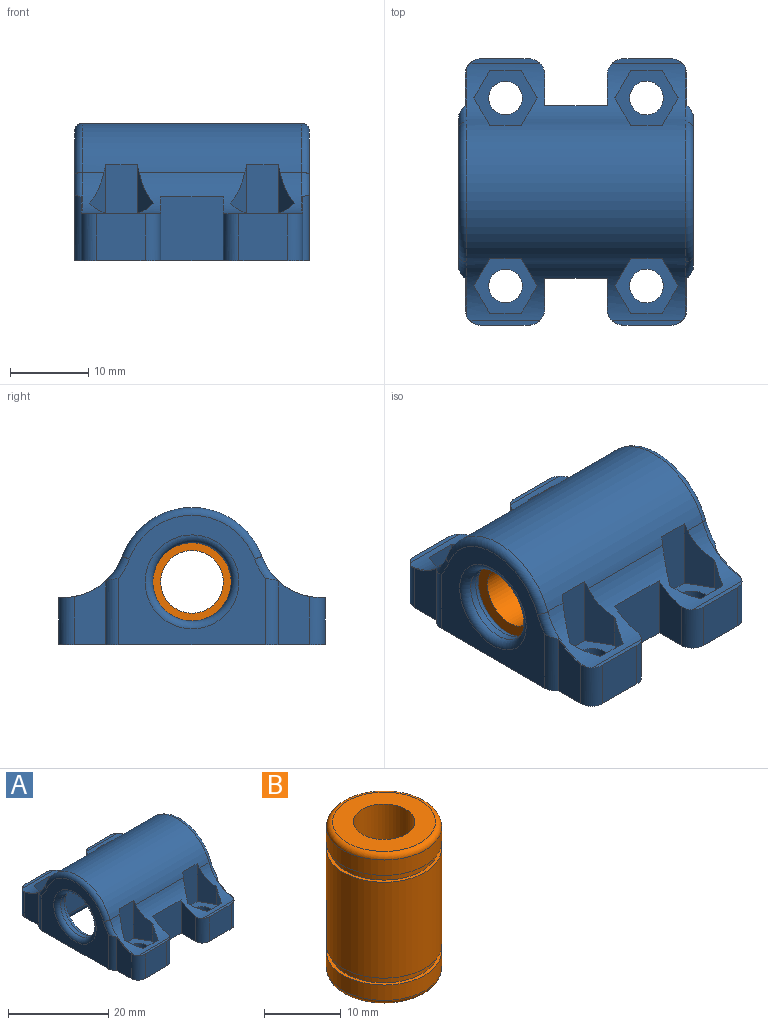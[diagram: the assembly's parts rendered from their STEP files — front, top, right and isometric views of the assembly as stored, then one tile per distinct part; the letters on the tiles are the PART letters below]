
ASSEMBLY  parts=2 mates=1
PART A: 94 faces, bbox 30x34x18.3 mm
  f0: cylinder r=2.15mm len=4.3mm, axis (0,0,-1), area 40.5mm2, adj f14,f88
  f1: cylinder r=2.15mm len=4.3mm, axis (0,0,-1), area 40.5mm2, adj f14,f61
  f2: cylinder r=2.15mm len=4.3mm, axis (0,0,-1), area 40.5mm2, adj f14,f74
  f3: cylinder r=2.15mm len=4.3mm, axis (0,0,-1), area 40.5mm2, adj f14,f75
  f4: plane 8.93x0.56mm, normal (0,0,1), area 4.5mm2, adj f7,f34,f38,f50
  f5: plane 8.93x0.56mm, normal (0,0,1), area 4.5mm2, adj f10,f42,f43,f49
  f6: plane 18.73x16.5mm, normal (-1,0,0), area 152.4mm2, adj f14,f36,f41,f51,f52,f53,f59
  f7: plane 6.15x6mm, normal (0,-1,0), area 36.9mm2, adj f4,f14,f34,f38
  f8: plane 6.15x6mm, normal (0,-1,0), area 36.9mm2, adj f13,f14,f35,f37
  f9: plane 18.73x16.5mm, normal (1,0,0), area 152.4mm2, adj f14,f33,f40,f54,f55,f56,f58
  f10: plane 6.15x6mm, normal (0,1,0), area 36.9mm2, adj f5,f14,f42,f43
  f11: plane 6.15x6mm, normal (0,1,0), area 36.9mm2, adj f12,f14,f39,f44
  f12: plane 8.93x0.56mm, normal (0,0,1), area 4.5mm2, adj f11,f39,f44,f49
  f13: plane 8.93x0.56mm, normal (0,0,1), area 4.5mm2, adj f8,f35,f37,f50
  f14: plane 34x30mm, normal (0,0,-1), area 298.4mm2, adj f0,f1,f2,f3,f6,f7,f8,f9
  f15: plane 24.2x6mm, normal (0,1,0), area 145.2mm2, adj f17,f20,f22,f47
  f16: plane 24.2x6mm, normal (0,-1,0), area 145.2mm2, adj f17,f20,f22,f46
  f17: cylinder r=7.55mm len=24.2mm, axis (-1,0,0), area 446.8mm2, adj f15,f16,f20,f22,f89,f90,f92,f93
  f18: cylinder r=9.5mm len=28mm, axis (-1,0,0), area 631.1mm2, adj f49,f50,f52,f55,f65,f66,f67,f71
  f19: cylinder r=5mm len=10mm, axis (-1,0,0), area 28.3mm2, adj f59,f60
  f20: plane 15.1x13.55mm, normal (1,0,0), area 67mm2, adj f15,f16,f17,f45,f60
  f21: cylinder r=5mm len=10mm, axis (1,0,0), area 28.3mm2, adj f57,f58
  f22: plane 15.1x13.55mm, normal (-1,0,0), area 67mm2, adj f15,f16,f17,f48,f57
  f23: plane 8.13x4mm, normal (1,0,0), area 27.6mm2, adj f14,f24,f43,f49
  f24: plane 8.13x8mm, normal (0,1,0), area 65.1mm2, adj f14,f23,f25,f49
  f25: plane 8.13x4mm, normal (-1,0,0), area 27.6mm2, adj f14,f24,f44,f49
  f26: plane 8.12x4mm, normal (1,0,0), area 27.5mm2, adj f14,f33,f34,f56
  f27: plane 8.12x4mm, normal (-1,0,0), area 27.5mm2, adj f14,f35,f36,f53
  f28: plane 8.13x4mm, normal (-1,0,0), area 27.6mm2, adj f14,f29,f38,f50
  f29: plane 8.13x8mm, normal (0,-1,0), area 65.1mm2, adj f14,f28,f30,f50
  f30: plane 8.13x4mm, normal (1,0,0), area 27.6mm2, adj f14,f29,f37,f50
  f31: plane 8.12x4mm, normal (1,0,0), area 27.5mm2, adj f14,f39,f40,f54
  f32: plane 8.12x4mm, normal (-1,0,0), area 27.5mm2, adj f14,f41,f42,f51
  f33: cylinder r=2mm len=8.44mm, axis (0,0,1), area 15.9mm2, adj f9,f14,f26,f56
  f34: cylinder r=2mm len=6.12mm, axis (0,0,-1), area 18.9mm2, adj f4,f7,f14,f26,f50,f56
  f35: cylinder r=2mm len=6.12mm, axis (0,0,1), area 18.9mm2, adj f8,f13,f14,f27,f50,f53
  f36: cylinder r=2mm len=8.44mm, axis (0,0,-1), area 15.9mm2, adj f6,f14,f27,f53
  f37: cylinder r=2mm len=6.13mm, axis (0,0,-1), area 18.9mm2, adj f8,f13,f14,f30,f50
  f38: cylinder r=2mm len=6.13mm, axis (0,0,1), area 18.9mm2, adj f4,f7,f14,f28,f50
  f39: cylinder r=2mm len=6.12mm, axis (0,0,-1), area 18.9mm2, adj f11,f12,f14,f31,f49,f54
  f40: cylinder r=2mm len=8.44mm, axis (0,0,-1), area 15.9mm2, adj f9,f14,f31,f54
  f41: cylinder r=2mm len=8.44mm, axis (0,0,1), area 15.9mm2, adj f6,f14,f32,f51
  f42: cylinder r=2mm len=6.12mm, axis (0,0,1), area 18.9mm2, adj f5,f10,f14,f32,f49,f51
  f43: cylinder r=2mm len=6.13mm, axis (0,0,-1), area 18.9mm2, adj f5,f10,f14,f23,f49
  f44: cylinder r=2mm len=6.13mm, axis (0,0,1), area 18.9mm2, adj f11,f12,f14,f25,f49
  f45: cylinder r=2mm len=19.1mm, axis (0,-1,0), area 52mm2, adj f14,f20,f46,f47
  f46: cylinder r=2mm len=28.2mm, axis (-1,0,0), area 80.6mm2, adj f14,f16,f45,f48
  f47: cylinder r=2mm len=28.2mm, axis (1,0,0), area 80.6mm2, adj f14,f15,f45,f48
  f48: cylinder r=2mm len=19.1mm, axis (0,-1,0), area 52mm2, adj f14,f22,f46,f47
  f49: cylinder r=8mm len=28mm, axis (-1,0,0), area 117.3mm2, adj f5,f12,f18,f23,f24,f25,f39,f42
  f50: cylinder r=8mm len=28mm, axis (-1,0,0), area 117.3mm2, adj f4,f13,f18,f28,f29,f30,f34,f35
  f51: torus R=9mm, axis (1,0,0), area 6mm2, adj f6,f32,f41,f42,f49,f52
  f52: torus R=8.5mm, axis (1,0,0), area 35mm2, adj f6,f18,f51,f53
  f53: torus R=9mm, axis (1,0,0), area 6mm2, adj f6,f27,f35,f36,f50,f52
  f54: torus R=9mm, axis (1,0,0), area 6mm2, adj f9,f31,f39,f40,f49,f55
  f55: torus R=8.5mm, axis (1,0,0), area 35mm2, adj f9,f18,f54,f56
  f56: torus R=9mm, axis (1,0,0), area 6mm2, adj f9,f26,f33,f34,f50,f55
  f57: torus R=6mm, axis (1,0,0), area 52.9mm2, adj f21,f22
  f58: torus R=6mm, axis (1,0,0), area 52.9mm2, adj f9,f21
  f59: torus R=6mm, axis (1,0,0), area 52.9mm2, adj f6,f19
  f60: torus R=6mm, axis (-1,0,0), area 52.9mm2, adj f19,f20
  f61: plane 8.08x7mm, normal (0,0,1), area 27.9mm2, adj f1,f62,f63,f64,f65,f66,f67
  f62: plane 4.34x3.5mm, normal (-0.87,0.5,0), area 14.3mm2, adj f50,f61,f63,f66
  f63: plane 4.04x3.06mm, normal (0,1,0), area 12.3mm2, adj f50,f61,f62,f64
  f64: plane 4.34x3.5mm, normal (0.87,0.5,0), area 14.3mm2, adj f50,f61,f63,f67
  f65: plane 9.24x4.04mm, normal (0,-1,0), area 37.4mm2, adj f18,f61,f66,f67
  f66: plane 9.26x3.52mm, normal (-0.87,-0.5,0), area 25.1mm2, adj f18,f50,f61,f62,f65
  f67: plane 9.26x3.52mm, normal (0.87,-0.5,0), area 25.1mm2, adj f18,f50,f61,f64,f65
  f68: plane 4.34x3.5mm, normal (0.87,0.5,0), area 14.3mm2, adj f50,f69,f72,f74
  f69: plane 4.04x3.06mm, normal (0,1,0), area 12.3mm2, adj f50,f68,f70,f74
  f70: plane 4.34x3.5mm, normal (-0.87,0.5,0), area 14.3mm2, adj f50,f69,f73,f74
  f71: plane 9.24x4.04mm, normal (0,-1,0), area 37.4mm2, adj f18,f72,f73,f74
  f72: plane 9.26x3.52mm, normal (0.87,-0.5,0), area 25.1mm2, adj f18,f50,f68,f71,f74
  f73: plane 9.26x3.52mm, normal (-0.87,-0.5,0), area 25.1mm2, adj f18,f50,f70,f71,f74
  f74: plane 8.08x7mm, normal (0,0,1), area 27.9mm2, adj f2,f68,f69,f70,f71,f72,f73
  f75: plane 8.08x7mm, normal (0,0,1), area 27.9mm2, adj f3,f76,f77,f78,f79,f80,f81
  f76: plane 4.34x3.5mm, normal (0.87,-0.5,0), area 14.3mm2, adj f49,f75,f77,f80
  f77: plane 4.04x3.06mm, normal (0,-1,0), area 12.3mm2, adj f49,f75,f76,f78
  f78: plane 4.34x3.5mm, normal (-0.87,-0.5,0), area 14.3mm2, adj f49,f75,f77,f81
  f79: plane 9.24x4.04mm, normal (0,1,0), area 37.4mm2, adj f18,f75,f80,f81
  f80: plane 9.26x3.52mm, normal (0.87,0.5,0), area 25.1mm2, adj f18,f49,f75,f76,f79
  f81: plane 9.26x3.52mm, normal (-0.87,0.5,0), area 25.1mm2, adj f18,f49,f75,f78,f79
  f82: plane 4.34x3.5mm, normal (-0.87,-0.5,0), area 14.3mm2, adj f49,f83,f86,f88
  f83: plane 4.04x3.06mm, normal (0,-1,0), area 12.3mm2, adj f49,f82,f84,f88
  f84: plane 4.34x3.5mm, normal (0.87,-0.5,0), area 14.3mm2, adj f49,f83,f87,f88
  f85: plane 9.24x4.04mm, normal (0,1,0), area 37.4mm2, adj f18,f86,f87,f88
  f86: plane 9.26x3.52mm, normal (-0.87,0.5,0), area 25.1mm2, adj f18,f49,f82,f85,f88
  f87: plane 9.26x3.52mm, normal (0.87,0.5,0), area 25.1mm2, adj f18,f49,f84,f85,f88
  f88: plane 8.08x7mm, normal (0,0,1), area 27.9mm2, adj f0,f82,f83,f84,f85,f86,f87
  f89: plane 5.64x1mm, normal (1,0,0), area 2.9mm2, adj f17,f91,f92,f93
  f90: plane 5.64x1mm, normal (-1,0,0), area 2.9mm2, adj f17,f91,f92,f93
  f91: plane 22x4.3mm, normal (0,0,-1), area 94.5mm2, adj f89,f90,f92,f93
  f92: plane 22x1mm, normal (0,-0.83,-0.56), area 26.5mm2, adj f17,f89,f90,f91
  f93: plane 22x1mm, normal (0,0.83,-0.56), area 26.5mm2, adj f17,f89,f90,f91
PART B: 14 faces, bbox 16.2x16.2x24 mm
  f0: cylinder r=7.5mm len=15mm, axis (0,0,-1), area 115.5mm2, adj f5,f12
  f1: cylinder r=4mm len=24mm, axis (0,0,-1), area 603.2mm2, adj f3,f4
  f2: cylinder r=7.5mm len=15mm, axis (0,0,-1), area 115.5mm2, adj f9,f13
  f3: plane 13.4x13.4mm, normal (0,0,1), area 90.8mm2, adj f1,f13
  f4: plane 13.4x13.4mm, normal (0,0,-1), area 90.8mm2, adj f1,f12
  f5: plane 15x15mm, normal (0,0,1), area 22.8mm2, adj f0,f6
  f6: cylinder r=7mm len=14mm, axis (0,0,1), area 48.4mm2, adj f5,f7
  f7: plane 15x15mm, normal (0,0,-1), area 22.8mm2, adj f6,f8
  f8: cylinder r=7.5mm len=15.3mm, axis (0,0,-1), area 721mm2, adj f7,f10
  f9: plane 15x15mm, normal (0,0,-1), area 22.8mm2, adj f2,f11
  f10: plane 15x15mm, normal (0,0,1), area 22.8mm2, adj f8,f11
  f11: cylinder r=7mm len=14mm, axis (0,0,1), area 48.4mm2, adj f9,f10
  f12: torus R=6.7mm, axis (0,0,1), area 56.9mm2, adj f0,f4
  f13: torus R=6.7mm, axis (0,0,1), area 56.9mm2, adj f2,f3
PLACE A at identity
PLACE B rot(axis=(0,1,0),90deg) t=(-12,0,8)mm
MATE fastened B.f0 <-> A.f19  axis (-1,0,0) through (0,0,8)mm
